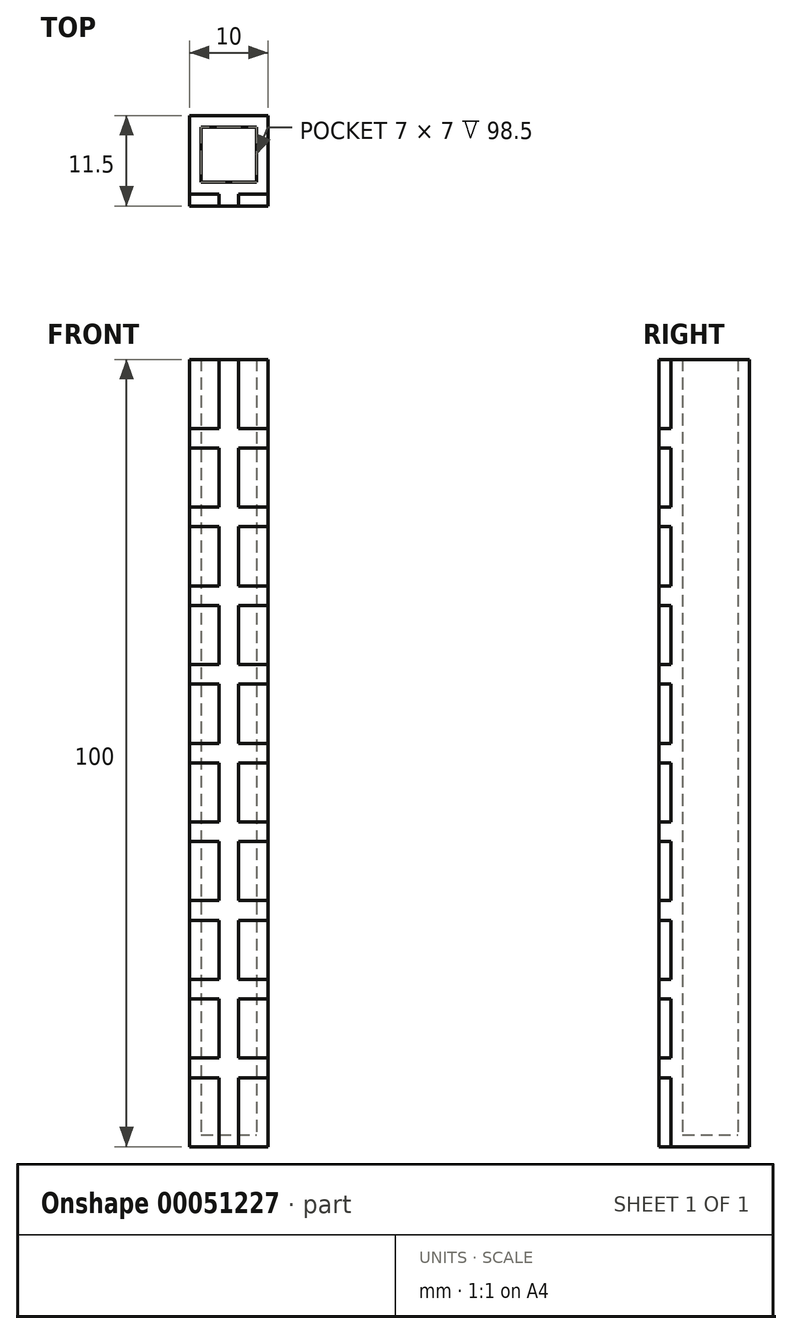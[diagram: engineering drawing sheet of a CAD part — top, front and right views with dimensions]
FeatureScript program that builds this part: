
annotation { "Feature Type Name" : "Feature", "Feature Type Description" : "" }
export const myFeature = defineFeature(function(context is Context, id is Id, definition is map)
    precondition{}
    {
        {
            var Q0;
            Q0=qCreatedBy(makeId("Top.planeOp"),FACE);
            var sketch = newSketch(context, id + "F0", { "sketchPlane" : qUnion([Q0])});
            skLineSegment(sketch, "E0.bottom", {"start": v(-5, -5) * mm, "end": v(5, -5) * mm});
            skLineSegment(sketch, "E0.top", {"start": v(-5, 5) * mm, "end": v(5, 5) * mm});
            skLineSegment(sketch, "E0.left", {"start": v(-5, -5) * mm, "end": v(-5, 5) * mm});
            skLineSegment(sketch, "E0.right", {"start": v(5, -5) * mm, "end": v(5, 5) * mm});
            skLineSegment(sketch, "E1", {"start": v(0, 0) * mm, "end": v(0, 5) * mm, "construction": true});
            skLineSegment(sketch, "E2", {"start": v(0, 0) * mm, "end": v(5, 0) * mm, "construction": true});
            skSolve(sketch);
        }
        {
            var Q0;
            Q0=makeQuery(id+"F0.imprint","IMPRINT",FACE,{"disambiguationData":[TD([[makeQuery(id+"F0.imprint","IMPRINT",EDGE,{"derivedFrom":sQuery(id+"F0.wireOp",EDGE,"E0.bottom")}),1.0]])]});
            var Q1;
            Q1 = qConstructionFilter(qBodyType(qCreatedBy(id + "F0" ,EDGE), BodyType.WIRE), ConstructionObject.NO);
            extrude(context, id + "F1", {"entities" : qUnion([Q0]), "surfaceEntities" : qUnion([Q1]), "depth" : 100 * mm});
        }
        {
            var Q0;
            Q0=makeQuery(id+"F1.opExtrude","CAP_FACE",FACE,{"disambiguationData":[OSD([sQuery(id+"F0.wireOp",EDGE,"E0.bottom"),sQuery(id+"F0.wireOp",EDGE,"E0.top"),sQuery(id+"F0.wireOp",EDGE,"E0.left"),sQuery(id+"F0.wireOp",EDGE,"E0.right")])],"isStart":false});
            shell(context, id + "F2", {"entities" : qUnion([Q0]), "thickness" : 1.5 * mm});
        }
        {
            var Q0;
            Q0=makeQuery(id+"F1.opExtrude","SWEPT_FACE",FACE,{"disambiguationData":[OSD([sQuery(id+"F0.wireOp",EDGE,"E0.bottom")])]});
            var sketch = newSketch(context, id + "F3", { "sketchPlane" : qUnion([Q0])});
            skLineSegment(sketch, "E3.bottom", {"start": v(-1.25, 100) * mm, "end": v(1.25, 100) * mm});
            skLineSegment(sketch, "E3.top", {"start": v(-1.25, 0) * mm, "end": v(1.25, 0) * mm});
            skLineSegment(sketch, "E3.left", {"start": v(-1.25, 100) * mm, "end": v(-1.25, 91.25) * mm});
            skLineSegment(sketch, "E3.right", {"start": v(1.25, 100) * mm, "end": v(1.25, 91.25) * mm});
            skLineSegment(sketch, "E4.bottom", {"start": v(-5, 91.25) * mm, "end": v(-1.25, 91.25) * mm});
            skLineSegment(sketch, "E4.top", {"start": v(-5, 88.75) * mm, "end": v(-1.25, 88.75) * mm});
            skLineSegment(sketch, "E4.left", {"start": v(-5, 91.25) * mm, "end": v(-5, 88.75) * mm});
            skLineSegment(sketch, "E4.right", {"start": v(5, 91.25) * mm, "end": v(5, 88.75) * mm});
            skLineSegment(sketch, "E5", {"start": v(-5, 90) * mm, "end": v(5, 90) * mm, "construction": true});
            skLineSegment(sketch, "E6.1.0.0", {"start": v(-5, 78.75) * mm, "end": v(-1.25, 78.75) * mm});
            skLineSegment(sketch, "E6.1.0.1", {"start": v(-5, 81.25) * mm, "end": v(-1.25, 81.25) * mm});
            skLineSegment(sketch, "E6.1.0.2", {"start": v(-5, 80) * mm, "end": v(5, 80) * mm, "construction": true});
            skLineSegment(sketch, "E6.1.0.3", {"start": v(-5, 81.25) * mm, "end": v(-5, 78.75) * mm});
            skLineSegment(sketch, "E6.1.0.4", {"start": v(5, 81.25) * mm, "end": v(5, 78.75) * mm});
            skLineSegment(sketch, "E6.2.0.0", {"start": v(-5, 68.75) * mm, "end": v(-1.25, 68.75) * mm});
            skLineSegment(sketch, "E6.2.0.1", {"start": v(-5, 71.25) * mm, "end": v(-1.25, 71.25) * mm});
            skLineSegment(sketch, "E6.2.0.2", {"start": v(-5, 70) * mm, "end": v(5, 70) * mm, "construction": true});
            skLineSegment(sketch, "E6.2.0.3", {"start": v(-5, 71.25) * mm, "end": v(-5, 68.75) * mm});
            skLineSegment(sketch, "E6.2.0.4", {"start": v(5, 71.25) * mm, "end": v(5, 68.75) * mm});
            skLineSegment(sketch, "E6.3.0.0", {"start": v(-5, 58.75) * mm, "end": v(-1.25, 58.75) * mm});
            skLineSegment(sketch, "E6.3.0.1", {"start": v(-5, 61.25) * mm, "end": v(-1.25, 61.25) * mm});
            skLineSegment(sketch, "E6.3.0.2", {"start": v(-5, 60) * mm, "end": v(5, 60) * mm, "construction": true});
            skLineSegment(sketch, "E6.3.0.3", {"start": v(-5, 61.25) * mm, "end": v(-5, 58.75) * mm});
            skLineSegment(sketch, "E6.3.0.4", {"start": v(5, 61.25) * mm, "end": v(5, 58.75) * mm});
            skLineSegment(sketch, "E6.4.0.0", {"start": v(-5, 48.75) * mm, "end": v(-1.25, 48.75) * mm});
            skLineSegment(sketch, "E6.4.0.1", {"start": v(-5, 51.25) * mm, "end": v(-1.25, 51.25) * mm});
            skLineSegment(sketch, "E6.4.0.2", {"start": v(-5, 50) * mm, "end": v(5, 50) * mm, "construction": true});
            skLineSegment(sketch, "E6.4.0.3", {"start": v(-5, 51.25) * mm, "end": v(-5, 48.75) * mm});
            skLineSegment(sketch, "E6.4.0.4", {"start": v(5, 51.25) * mm, "end": v(5, 48.75) * mm});
            skLineSegment(sketch, "E6.5.0.0", {"start": v(-5, 38.75) * mm, "end": v(-1.25, 38.75) * mm});
            skLineSegment(sketch, "E6.5.0.1", {"start": v(-5, 41.25) * mm, "end": v(-1.25, 41.25) * mm});
            skLineSegment(sketch, "E6.5.0.2", {"start": v(-5, 40) * mm, "end": v(5, 40) * mm, "construction": true});
            skLineSegment(sketch, "E6.5.0.3", {"start": v(-5, 41.25) * mm, "end": v(-5, 38.75) * mm});
            skLineSegment(sketch, "E6.5.0.4", {"start": v(5, 41.25) * mm, "end": v(5, 38.75) * mm});
            skLineSegment(sketch, "E6.6.0.0", {"start": v(-5, 28.75) * mm, "end": v(-1.25, 28.75) * mm});
            skLineSegment(sketch, "E6.6.0.1", {"start": v(-5, 31.25) * mm, "end": v(-1.25, 31.25) * mm});
            skLineSegment(sketch, "E6.6.0.2", {"start": v(-5, 30) * mm, "end": v(5, 30) * mm, "construction": true});
            skLineSegment(sketch, "E6.6.0.3", {"start": v(-5, 31.25) * mm, "end": v(-5, 28.75) * mm});
            skLineSegment(sketch, "E6.6.0.4", {"start": v(5, 31.25) * mm, "end": v(5, 28.75) * mm});
            skLineSegment(sketch, "E6.7.0.0", {"start": v(-5, 18.75) * mm, "end": v(-1.25, 18.75) * mm});
            skLineSegment(sketch, "E6.7.0.1", {"start": v(-5, 21.25) * mm, "end": v(-1.25, 21.25) * mm});
            skLineSegment(sketch, "E6.7.0.2", {"start": v(-5, 20) * mm, "end": v(5, 20) * mm, "construction": true});
            skLineSegment(sketch, "E6.7.0.3", {"start": v(-5, 21.25) * mm, "end": v(-5, 18.75) * mm});
            skLineSegment(sketch, "E6.7.0.4", {"start": v(5, 21.25) * mm, "end": v(5, 18.75) * mm});
            skLineSegment(sketch, "E6.8.0.0", {"start": v(-5, 8.75) * mm, "end": v(-1.25, 8.75) * mm});
            skLineSegment(sketch, "E6.8.0.1", {"start": v(-5, 11.25) * mm, "end": v(-1.25, 11.25) * mm});
            skLineSegment(sketch, "E6.8.0.2", {"start": v(-5, 10) * mm, "end": v(5, 10) * mm, "construction": true});
            skLineSegment(sketch, "E6.8.0.3", {"start": v(-5, 11.25) * mm, "end": v(-5, 8.75) * mm});
            skLineSegment(sketch, "E6.8.0.4", {"start": v(5, 11.25) * mm, "end": v(5, 8.75) * mm});
            skLineSegment(sketch, "E6.9.0.2", {"start": v(-5, 0) * mm, "end": v(5, 0) * mm, "construction": true});
            skLineSegment(sketch, "E6.direction1", {"start": v(-5, 88.75) * mm, "end": v(-5, 78.75) * mm, "construction": true});
            skLineSegment(sketch, "E7.trimOffspring", {"start": v(-1.25, 8.75) * mm, "end": v(-1.25, 0) * mm});
            skLineSegment(sketch, "E8.trimOffspring", {"start": v(1.25, 8.75) * mm, "end": v(1.25, 0) * mm});
            skLineSegment(sketch, "E9.trimOffspring", {"start": v(1.25, 11.25) * mm, "end": v(5, 11.25) * mm});
            skLineSegment(sketch, "E10.trimOffspring", {"start": v(1.25, 18.75) * mm, "end": v(5, 18.75) * mm});
            skLineSegment(sketch, "E11.trimOffspring", {"start": v(-1.25, 18.75) * mm, "end": v(-1.25, 11.25) * mm});
            skLineSegment(sketch, "E12.trimOffspring", {"start": v(1.25, 18.75) * mm, "end": v(1.25, 11.25) * mm});
            skLineSegment(sketch, "E13.trimOffspring", {"start": v(1.25, 21.25) * mm, "end": v(5, 21.25) * mm});
            skLineSegment(sketch, "E14.trimOffspring", {"start": v(1.25, 8.75) * mm, "end": v(5, 8.75) * mm});
            skLineSegment(sketch, "E15.trimOffspring", {"start": v(1.25, 28.75) * mm, "end": v(1.25, 21.25) * mm});
            skLineSegment(sketch, "E16.trimOffspring", {"start": v(1.25, 28.75) * mm, "end": v(5, 28.75) * mm});
            skLineSegment(sketch, "E17.trimOffspring", {"start": v(-1.25, 28.75) * mm, "end": v(-1.25, 21.25) * mm});
            skLineSegment(sketch, "E18.trimOffspring", {"start": v(1.25, 31.25) * mm, "end": v(5, 31.25) * mm});
            skLineSegment(sketch, "E19.trimOffspring", {"start": v(1.25, 38.75) * mm, "end": v(5, 38.75) * mm});
            skLineSegment(sketch, "E20.trimOffspring", {"start": v(-1.25, 38.75) * mm, "end": v(-1.25, 31.25) * mm});
            skLineSegment(sketch, "E21.trimOffspring", {"start": v(1.25, 41.25) * mm, "end": v(5, 41.25) * mm});
            skLineSegment(sketch, "E22.trimOffspring", {"start": v(1.25, 38.75) * mm, "end": v(1.25, 31.25) * mm});
            skLineSegment(sketch, "E23.trimOffspring", {"start": v(1.25, 48.75) * mm, "end": v(5, 48.75) * mm});
            skLineSegment(sketch, "E24.trimOffspring", {"start": v(-1.25, 48.75) * mm, "end": v(-1.25, 41.25) * mm});
            skLineSegment(sketch, "E25.trimOffspring", {"start": v(1.25, 51.25) * mm, "end": v(5, 51.25) * mm});
            skLineSegment(sketch, "E26.trimOffspring", {"start": v(1.25, 48.75) * mm, "end": v(1.25, 41.25) * mm});
            skLineSegment(sketch, "E27.trimOffspring", {"start": v(1.25, 58.75) * mm, "end": v(5, 58.75) * mm});
            skLineSegment(sketch, "E28.trimOffspring", {"start": v(1.25, 61.25) * mm, "end": v(5, 61.25) * mm});
            skLineSegment(sketch, "E29.trimOffspring", {"start": v(-1.25, 58.75) * mm, "end": v(-1.25, 51.25) * mm});
            skLineSegment(sketch, "E30.trimOffspring", {"start": v(1.25, 58.75) * mm, "end": v(1.25, 51.25) * mm});
            skLineSegment(sketch, "E31.trimOffspring", {"start": v(1.25, 68.75) * mm, "end": v(5, 68.75) * mm});
            skLineSegment(sketch, "E32.trimOffspring", {"start": v(-1.25, 68.75) * mm, "end": v(-1.25, 61.25) * mm});
            skLineSegment(sketch, "E33.trimOffspring", {"start": v(1.25, 71.25) * mm, "end": v(5, 71.25) * mm});
            skLineSegment(sketch, "E34.trimOffspring", {"start": v(1.25, 68.75) * mm, "end": v(1.25, 61.25) * mm});
            skLineSegment(sketch, "E35.trimOffspring", {"start": v(1.25, 78.75) * mm, "end": v(5, 78.75) * mm});
            skLineSegment(sketch, "E36.trimOffspring", {"start": v(1.25, 81.25) * mm, "end": v(5, 81.25) * mm});
            skLineSegment(sketch, "E37.trimOffspring", {"start": v(-1.25, 78.75) * mm, "end": v(-1.25, 71.25) * mm});
            skLineSegment(sketch, "E38.trimOffspring", {"start": v(1.25, 78.75) * mm, "end": v(1.25, 71.25) * mm});
            skLineSegment(sketch, "E39.trimOffspring", {"start": v(1.25, 88.75) * mm, "end": v(5, 88.75) * mm});
            skLineSegment(sketch, "E40.trimOffspring", {"start": v(1.25, 91.25) * mm, "end": v(5, 91.25) * mm});
            skLineSegment(sketch, "E41.trimOffspring", {"start": v(1.25, 88.75) * mm, "end": v(1.25, 81.25) * mm});
            skLineSegment(sketch, "E42.trimOffspring", {"start": v(-1.25, 88.75) * mm, "end": v(-1.25, 81.25) * mm});
            skSolve(sketch);
        }
        {
            var Q0;
            Q0 = qSketchRegion(id + "F3", true);
            extrude(context, id + "F4", {"entities" : qUnion([Q0]), "operationType" : NewBodyOperationType.ADD, "depth" : 1.5 * mm});
        }
    });
